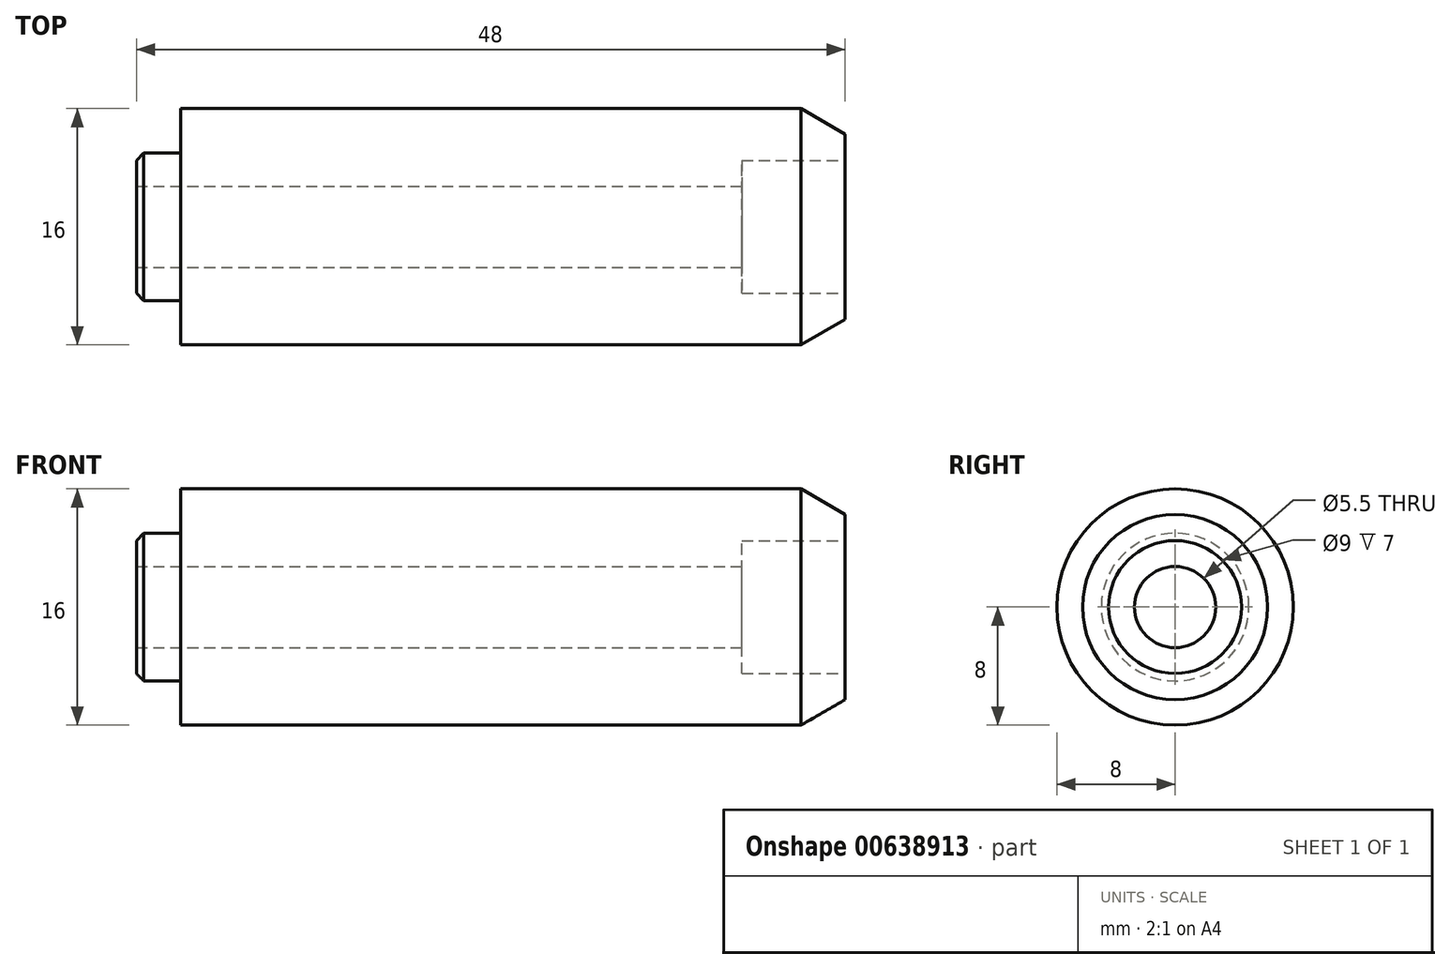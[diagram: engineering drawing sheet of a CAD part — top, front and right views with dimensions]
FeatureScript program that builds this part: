
annotation { "Feature Type Name" : "Feature", "Feature Type Description" : "" }
export const myFeature = defineFeature(function(context is Context, id is Id, definition is map)
    precondition{}
    {
        {
            var Q0;
            Q0=qCreatedBy(makeId("Front.planeOp"),FACE);
            var sketch = newSketch(context, id + "F0", { "sketchPlane" : qUnion([Q0])});
            skLineSegment(sketch, "E0", {"start": v(112.96, 0) * mm, "end": v(92.96, 0) * mm});
            skLineSegment(sketch, "E1", {"start": v(102.96, 10) * mm, "end": v(102.96, -10) * mm});
            skCircle(sketch, "E2", {"center": v(102.96, 0) * mm, "radius": 6.27 * mm});
            skCircle(sketch, "E3", {"center": v(102.96, 0) * mm, "radius": 8 * mm});
            skLineSegment(sketch, "E4", {"start": v(-71.96, -2.75) * mm, "end": v(-109.96, -2.75) * mm});
            skLineSegment(sketch, "E5", {"start": v(-71.96, 2.75) * mm, "end": v(-109.96, 2.75) * mm});
            skLineSegment(sketch, "E6", {"start": v(-64.96, 4.5) * mm, "end": v(-71.96, 4.5) * mm});
            skLineSegment(sketch, "E7", {"start": v(-64.96, -4.5) * mm, "end": v(-71.96, -4.5) * mm});
            skLineSegment(sketch, "E8", {"start": v(-71.96, 4.5) * mm, "end": v(-71.96, -4.5) * mm});
            skLineSegment(sketch, "E9", {"start": v(-62.96, 0) * mm, "end": v(-81.96, 0) * mm});
            skLineSegment(sketch, "E10", {"start": v(-64.96, 0) * mm, "end": v(-112.96, 0) * mm});
            skLineSegment(sketch, "E11", {"start": v(-112.46, 5) * mm, "end": v(-112.46, -5) * mm});
            skLineSegment(sketch, "E12", {"start": v(-112.96, 4.5) * mm, "end": v(-112.46, 5) * mm});
            skLineSegment(sketch, "E13", {"start": v(-112.96, -4.5) * mm, "end": v(-112.46, -5) * mm});
            skLineSegment(sketch, "E14", {"start": v(-112.46, 5) * mm, "end": v(-109.96, 5) * mm});
            skLineSegment(sketch, "E15", {"start": v(-112.46, -5) * mm, "end": v(-109.96, -5) * mm});
            skLineSegment(sketch, "E16", {"start": v(-112.96, 4.5) * mm, "end": v(-112.96, -4.5) * mm});
            skLineSegment(sketch, "E17", {"start": v(-67.96, -8) * mm, "end": v(-109.96, -8) * mm});
            skLineSegment(sketch, "E18", {"start": v(-109.96, 8) * mm, "end": v(-109.96, -8) * mm});
            skLineSegment(sketch, "E19", {"start": v(-67.96, 8) * mm, "end": v(-109.96, 8) * mm});
            skLineSegment(sketch, "E20", {"start": v(-64.96, 6.27) * mm, "end": v(-64.96, -6.27) * mm});
            skLineSegment(sketch, "E21", {"start": v(-67.96, 8) * mm, "end": v(-64.96, 6.27) * mm});
            skLineSegment(sketch, "E22", {"start": v(-67.96, -8) * mm, "end": v(-64.96, -6.27) * mm});
            skLineSegment(sketch, "E23", {"start": v(-67.96, 8) * mm, "end": v(-67.96, -8) * mm});
            skCircle(sketch, "E24", {"center": v(102.96, 0) * mm, "radius": 4.5 * mm});
            skCircle(sketch, "E25", {"center": v(102.96, 0) * mm, "radius": 2.75 * mm});
            skSolve(sketch);
        }
        {
            var Q0;
            {var subQ0=sQuery(id+"F0.wireOp",EDGE,"E8");var subQ6=sQuery(id+"F0.wireOp",EDGE,"E6");var subQ7=makeQuery(id+"F0.imprint","INTERSECT",VERTEX,{"derivedFrom":[subQ6,subQ0]});Q0=makeQuery(id+"F0.imprint","IMPRINT",FACE,{"disambiguationData":[TD([[makeQuery(id+"F0.imprint","IMPRINT",EDGE,{"disambiguationData":[TD([[subQ7,1.0]])],"derivedFrom":subQ6}),1.0]])]});}
            var Q1;
            {var subQ5=sQuery(id+"F0.wireOp",EDGE,"E21");Q1=makeQuery(id+"F0.imprint","IMPRINT",FACE,{"disambiguationData":[TD([[makeQuery(id+"F0.imprint","IMPRINT",EDGE,{"derivedFrom":subQ5}),-1.0]])]});}
            var Q2;
            {var subQ0=sQuery(id+"F0.wireOp",EDGE,"E20");var subQ1=sQuery(id+"F0.wireOp",EDGE,"E6");var subQ2=makeQuery(id+"F0.imprint","INTERSECT",VERTEX,{"derivedFrom":[subQ1,subQ0]});Q2=makeQuery(id+"F0.imprint","IMPRINT",FACE,{"disambiguationData":[TD([[makeQuery(id+"F0.imprint","IMPRINT",EDGE,{"disambiguationData":[TD([[subQ2,-1.0]])],"derivedFrom":subQ1}),1.0]])]});}
            var Q3;
            {var subQ0=sQuery(id+"F0.wireOp",EDGE,"E14");Q3=makeQuery(id+"F0.imprint","IMPRINT",FACE,{"disambiguationData":[TD([[makeQuery(id+"F0.imprint","IMPRINT",EDGE,{"derivedFrom":subQ0}),-1.0]])]});}
            var Q4;
            {var subQ8=sQuery(id+"F0.wireOp",EDGE,"E5");Q4=makeQuery(id+"F0.imprint","IMPRINT",FACE,{"disambiguationData":[TD([[makeQuery(id+"F0.imprint","IMPRINT",EDGE,{"derivedFrom":subQ8}),-1.0]])]});}
            var Q5;
            {var subQ5=sQuery(id+"F0.wireOp",EDGE,"E12");Q5=makeQuery(id+"F0.imprint","IMPRINT",FACE,{"disambiguationData":[TD([[makeQuery(id+"F0.imprint","IMPRINT",EDGE,{"derivedFrom":subQ5}),-1.0]])]});}
            var Q6;
            {var subQ6=sQuery(id+"F0.wireOp",EDGE,"E5");Q6=makeQuery(id+"F0.imprint","IMPRINT",FACE,{"disambiguationData":[TD([[makeQuery(id+"F0.imprint","IMPRINT",EDGE,{"derivedFrom":subQ6}),1.0]])]});}
            var Q7;
            Q7=sQuery(id+"F0.wireOp",EDGE,"E10");
            revolve(context, id + "F1", {"entities" : qUnion([Q0, Q1, Q2, Q3, Q4, Q5, Q6]), "axis" : qUnion([Q7]), "revolveType" : RevolveType.FULL});
        }
        {
            var Q0;
            Q0=makeQuery(id+"F1.opRevolve","SWEPT_FACE",FACE,{"disambiguationData":[OSD([sQuery(id+"F0.wireOp",EDGE,"E20")])]});
            var sketch = newSketch(context, id + "F2", { "sketchPlane" : qUnion([Q0])});
            skCircle(sketch, "E26.0", {"center": v(0, 0) * mm, "radius": 6.27 * mm});
            skSolve(sketch);
        }
        {
            var Q0;
            Q0=sQuery(id+"F2.wireOp",VERTEX,"E26.0.center");
            var Q1;
            Q1=makeQuery(id+"F1.opRevolve","SWEPT_BODY",BODY,{"disambiguationData":[OSD([sQuery(id+"F0.wireOp",EDGE,"E10"),sQuery(id+"F0.wireOp",EDGE,"E12"),sQuery(id+"F0.wireOp",EDGE,"E14"),sQuery(id+"F0.wireOp",EDGE,"E16"),sQuery(id+"F0.wireOp",EDGE,"E18"),sQuery(id+"F0.wireOp",EDGE,"E19"),sQuery(id+"F0.wireOp",EDGE,"E20"),sQuery(id+"F0.wireOp",EDGE,"E21")])]});
            hole(context, id + "F3", {"style" : HoleStyle.C_BORE, "endStyle" : HoleEndStyle.THROUGH, "holeDiameter" : 5.5 * mm, "cBoreDiameter" : 9 * mm, "cBoreDepth" : 7 * mm, "majorDiameter" : 5 * mm, "isTappedThrough" : true, "tappedDepth" : 12 * mm, "tapClearance" : 3, "locations" : qUnion([Q0]), "scope" : qUnion([Q1])});
        }
    });
